# Revit family: Legrand_Emergencia_B65LED_EN
name_source: partatom
category: Luminaires
units: mm (PartAtom-declared; Revit-internal decimal feet)

## family parameters
Cote de connecteur circulaire = Utiliser le diamètre
Couper avec des vides une fois chargée = Non
Hôte = Face
Partagée = Non
Point de calcul de pièce = Non
Source d'éclairage = Oui
Type d'élément = Normal

## types (8) — shared parameters
Angle de l'inclinaison = 90.00°
BAES_FULL_WARRANTY_PERIOD = 2
CATEGORY = Self-contained
COLOUR_HOUSING = Grey
DEGREE_OF_PROTECTION_(IP) = IP65
Elévation par défaut = 1219 mm
FUNCTION = EL unit
Filtre de couleur = 16777215
General Conditions of Use = https://export.legrand.com
Gradation des changements de température de couleur de lampe = <Aucun>
HEIGHT/DEPTH = 59.7
LABELLING_TYPE = Sticker
LAMP_TYPE = LED not exchangeable
LENGTH = 280
MATERIAL_COVER = Plastic. opal
MATERIAL_HOUSING = Plastic
MOUNTING_METHOD = Built-in
NOMINAL_VOLTAGE_(MAX) = 230
NOMINAL_VOLTAGE_(MIN) = 230
POWER_SUPPLY_SYSTEM = Peripheral (individual battery)
PRODUCT_FORMAT = Rectangle
PROTECTION_CLASS = II
VOLTAGE_TYPE = AC
WIDTH = 120

## per-type parameters (varying)
| type | ARTICLE_NUMBER | AUTONOMY | BATTERY_QUALITY | Fichier de distribution photométrique | LAMP_POWER | LUMINOUS_FLUX_AT_EMERGENCY_OPERATION | MONITORING_EQUIPEMENT | REF_SPARE_BATTERY | WIRING_SYSTEM |
| B65 LED M-NM 100LM 1H IP55 STD | 661431 | 1 | NiCd | 661431.ies | 10 | 100 | None | 660972 | Continuous circuit/emergency cicuit |
| B65 LED M-NM 200LM 1H IP55 STD | 661433 | 1 | NiCd | 661433.ies | 20 | 200 | None | 660962 | Continuous circuit/emergency cicuit |
| B65 LED M-NM 350LM 1H IP55 STD | 661434 | 1 | NiCd | 661434.ies | 35 | 350 | None | 660962 | Continuous circuit/emergency cicuit |
| B65 LED M-NM 100LM 3H IP55 STD | 661440 | 3 | NiMh | 661440.ies | 10 | 100 | None | 660971 | Standby switching |
| B65 LED M-NM 100LM 1H IP55 ADR | 662431 | 1 | NiCd | 662431.ies | 10 | 100 | Automatic self test | 660972 | Continuous circuit/emergency cicuit |
| B65 LED M-NM 200LM 1H IP55 ADR | 662433 | 1 | NiCd | 662433.ies | 20 | 200 | Automatic self test | 660962 | Continuous circuit/emergency cicuit |
| B65 LED M-NM 350LM 1H IP55 ADR | 662434 | 1 | NiMh | 662434.ies | 35 | 350 | Automatic self test | 660971 | Continuous circuit/emergency cicuit |
| B65 LED M-NM 100LM 3H IP55 ADR | 662440 | 3 | NiMh | 662440.ies | 10 | 100 | Automatic self test | 660971 | Continuous circuit/emergency cicuit |

note: column(s) folded — value = type name in every type: DESCRIPTION
